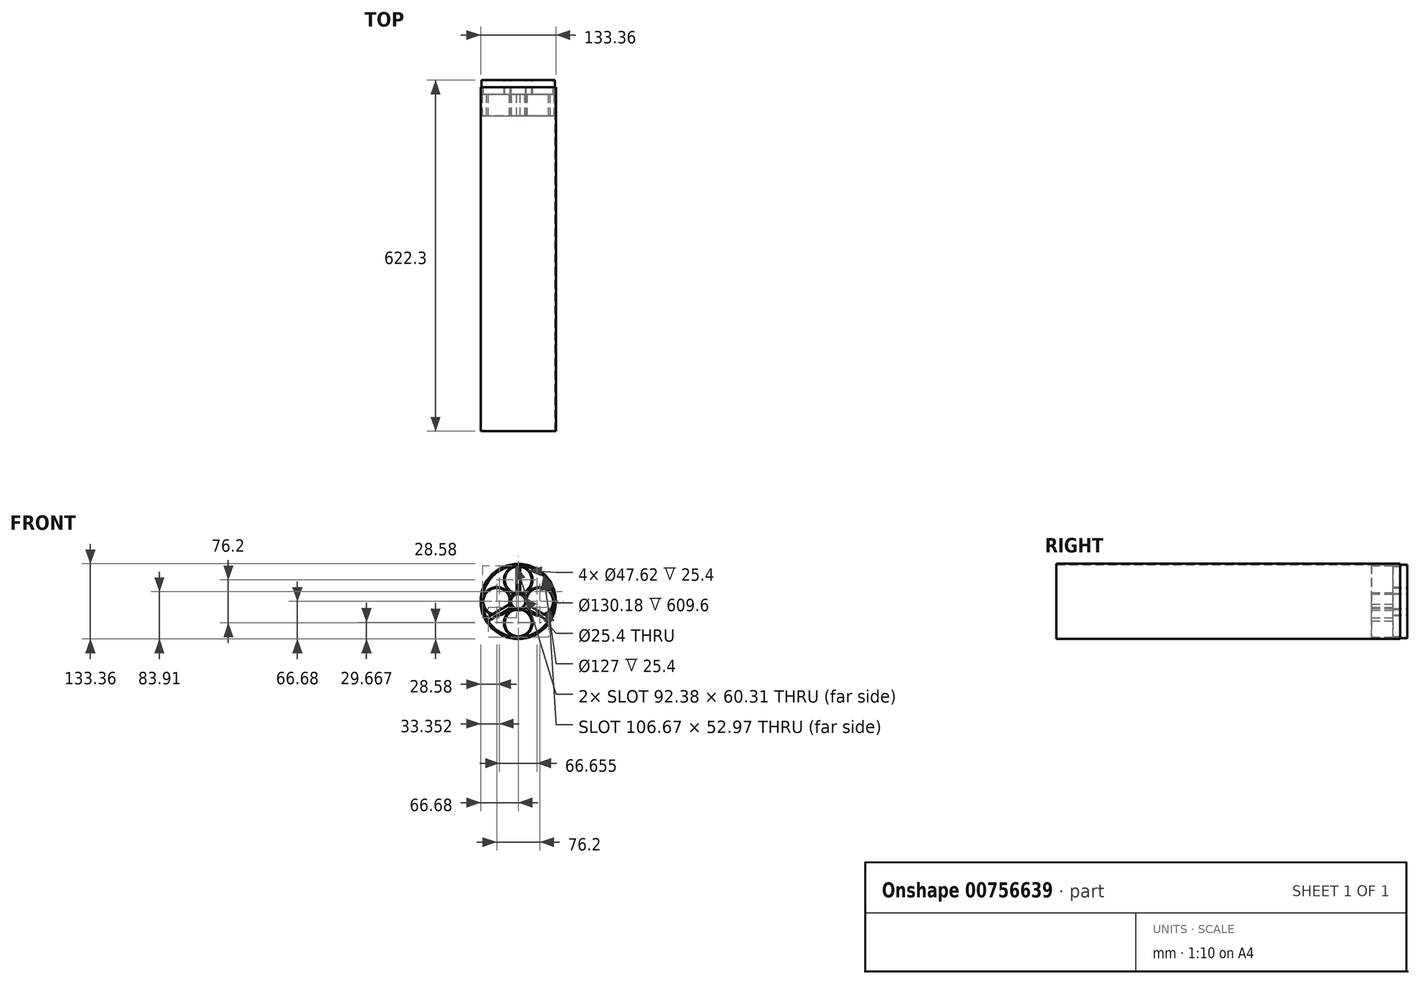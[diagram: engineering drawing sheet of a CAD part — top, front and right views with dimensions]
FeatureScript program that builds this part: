
annotation { "Feature Type Name" : "Feature", "Feature Type Description" : "" }
export const myFeature = defineFeature(function(context is Context, id is Id, definition is map)
    precondition{}
    {
        {
            var Q0;
            Q0=qCreatedBy(makeId("Front.planeOp"),FACE);
            var sketch = newSketch(context, id + "F0", { "sketchPlane" : qUnion([Q0])});
            skCircle(sketch, "E0", {"center": v(0, 0) * mm, "radius": 63.5 * mm});
            skCircle(sketch, "E1", {"center": v(0, 0) * mm, "radius": 12.7 * mm});
            skLineSegment(sketch, "E2", {"start": v(0, 63.5) * mm, "end": v(0, 12.7) * mm});
            skCircle(sketch, "E3", {"center": v(0, 38.1) * mm, "radius": 25.4 * mm});
            skCircle(sketch, "E4.1.0", {"center": v(-38.1, 0) * mm, "radius": 25.4 * mm});
            skCircle(sketch, "E4.2.0", {"center": v(0, -38.1) * mm, "radius": 25.4 * mm});
            skCircle(sketch, "E4.3.0", {"center": v(38.1, 0) * mm, "radius": 25.4 * mm});
            skCircle(sketch, "E5.0", {"center": v(0, 0) * mm, "radius": 65.09 * mm});
            skCircle(sketch, "E6.0", {"center": v(-38.1, 0) * mm, "radius": 23.81 * mm});
            skCircle(sketch, "E7.0", {"center": v(0, 38.1) * mm, "radius": 23.81 * mm});
            skCircle(sketch, "E8.0", {"center": v(38.1, 0) * mm, "radius": 23.81 * mm});
            skCircle(sketch, "E9.0", {"center": v(0, -38.1) * mm, "radius": 23.81 * mm});
            skCircle(sketch, "E10.0", {"center": v(0, 0) * mm, "radius": 66.68 * mm});
            skSolve(sketch);
        }
        {
            var Q0;
            {var subQ1=sQuery(id+"F0.wireOp",EDGE,"E2");var subQ3=sQuery(id+"F0.wireOp",EDGE,"E7.0");var subQ4=makeQuery(id+"F0.imprint","INTERSECT",VERTEX,{"disambiguationData":[OD(0.0)],"derivedFrom":[subQ1,subQ3]});Q0=makeQuery(id+"F0.imprint","IMPRINT",FACE,{"disambiguationData":[TD([[makeQuery(id+"F0.imprint","IMPRINT",EDGE,{"disambiguationData":[TD([[subQ4,1.0]])],"derivedFrom":subQ3}),-1.0]])]});}
            var Q1;
            Q1=makeQuery(id+"F0.imprint","IMPRINT",FACE,{"disambiguationData":[TD([[makeQuery(id+"F0.imprint","IMPRINT",EDGE,{"derivedFrom":sQuery(id+"F0.wireOp",EDGE,"E8.0")}),-1.0]])]});
            var Q2;
            Q2=makeQuery(id+"F0.imprint","IMPRINT",FACE,{"disambiguationData":[TD([[makeQuery(id+"F0.imprint","IMPRINT",EDGE,{"derivedFrom":sQuery(id+"F0.wireOp",EDGE,"E9.0")}),-1.0]])]});
            var Q3;
            {var subQ1=sQuery(id+"F0.wireOp",EDGE,"E2");var subQ3=sQuery(id+"F0.wireOp",EDGE,"E7.0");var subQ4=makeQuery(id+"F0.imprint","INTERSECT",VERTEX,{"disambiguationData":[OD(0.0)],"derivedFrom":[subQ1,subQ3]});Q3=makeQuery(id+"F0.imprint","IMPRINT",FACE,{"disambiguationData":[TD([[makeQuery(id+"F0.imprint","IMPRINT",EDGE,{"disambiguationData":[TD([[subQ4,-1.0]])],"derivedFrom":subQ3}),-1.0]])]});}
            var Q4;
            Q4=makeQuery(id+"F0.imprint","IMPRINT",FACE,{"disambiguationData":[TD([[makeQuery(id+"F0.imprint","IMPRINT",EDGE,{"derivedFrom":sQuery(id+"F0.wireOp",EDGE,"E6.0")}),-1.0]])]});
            var Q5;
            Q5=makeQuery(id+"F0.imprint","IMPRINT",FACE,{"disambiguationData":[TD([[makeQuery(id+"F0.imprint","IMPRINT",EDGE,{"derivedFrom":sQuery(id+"F0.wireOp",EDGE,"E5.0")}),1.0]])]});
            extrude(context, id + "F1", {"entities" : qUnion([Q0, Q1, Q2, Q3, Q4, Q5]), "endBound" : BoundingType.SYMMETRIC, "depth" : 25.4 * mm, "offsetDistance" : 25.4 * mm});
        }
        {
            var Q0;
            Q0=qCreatedBy(makeId("Front.planeOp"),FACE);
            var sketch = newSketch(context, id + "F2", { "sketchPlane" : qUnion([Q0])});
            skArc(sketch, "E11", {"start": v(-53.34, -34.46) * mm, "mid": v(0, -63.5) * mm, "end": v(53.34, -34.46) * mm});
            skCircle(sketch, "E12", {"center": v(0, 0) * mm, "radius": 12.7 * mm});
            skCircle(sketch, "E13.0", {"center": v(0, 0) * mm, "radius": 65.09 * mm});
            skLineSegment(sketch, "E14.0", {"start": v(-53.4, -34.5) * mm, "end": v(-11.88, -10.53) * mm});
            skLineSegment(sketch, "E15.0", {"start": v(-56.58, -29) * mm, "end": v(-15.06, -5.03) * mm});
            skLineSegment(sketch, "E16.0", {"start": v(56.58, -29) * mm, "end": v(15.06, -5.03) * mm});
            skLineSegment(sketch, "E17.0", {"start": v(53.4, -34.5) * mm, "end": v(11.88, -10.53) * mm});
            skLineSegment(sketch, "E18.0", {"start": v(-3.17, 63.5) * mm, "end": v(-3.17, 15.55) * mm});
            skLineSegment(sketch, "E19.0", {"start": v(3.18, 63.5) * mm, "end": v(3.18, 15.55) * mm});
            skArc(sketch, "E20.0", {"start": v(-11.88, -10.53) * mm, "mid": v(0, -15.88) * mm, "end": v(11.88, -10.53) * mm});
            skPoint(sketch, "E21.orphan", {"position": v(-55, -31.75) * mm});
            skPoint(sketch, "E22.orphan", {"position": v(55, -31.75) * mm});
            skPoint(sketch, "E23.orphan", {"position": v(0, 63.5) * mm});
            skArc(sketch, "E24.trimOffspring", {"start": v(-3.17, 15.55) * mm, "mid": v(-13.75, 7.94) * mm, "end": v(-15.06, -5.03) * mm});
            skArc(sketch, "E25.trimOffspring", {"start": v(-3.17, 63.42) * mm, "mid": v(-55, 31.75) * mm, "end": v(-56.51, -28.96) * mm});
            skArc(sketch, "E26.trimOffspring", {"start": v(15.06, -5.03) * mm, "mid": v(13.75, 7.94) * mm, "end": v(3.18, 15.55) * mm});
            skArc(sketch, "E27.trimOffspring", {"start": v(56.51, -28.96) * mm, "mid": v(55, 31.75) * mm, "end": v(3.18, 63.42) * mm});
            skSolve(sketch);
        }
        {
            var Q0;
            Q0=makeQuery(id+"F2.imprint","IMPRINT",FACE,{"disambiguationData":[TD([[makeQuery(id+"F2.imprint","IMPRINT",EDGE,{"derivedFrom":sQuery(id+"F2.wireOp",EDGE,"E12")}),1.0]])]});
            extrude(context, id + "F3", {"entities" : qUnion([Q0]), "depth" : 50.8 * mm, "offsetDistance" : 25.4 * mm});
        }
        {
            var Q0;
            {var subQ8=sQuery(id+"F2.wireOp",EDGE,"E11");Q0=makeQuery(id+"F2.imprint","IMPRINT",FACE,{"disambiguationData":[TD([[makeQuery(id+"F2.imprint","IMPRINT",EDGE,{"derivedFrom":subQ8}),-1.0]])]});}
            extrude(context, id + "F4", {"entities" : qUnion([Q0]), "depth" : 50.8 * mm, "offsetDistance" : 25.4 * mm, "hasSecondDirection" : true, "secondDirectionOppositeDirection" : false, "secondDirectionDepth" : 12.7 * mm});
        }
        {
            var Q0;
            Q0=makeQuery(id+"F0.imprint","IMPRINT",FACE,{"disambiguationData":[TD([[makeQuery(id+"F0.imprint","IMPRINT",EDGE,{"derivedFrom":sQuery(id+"F0.wireOp",EDGE,"E5.0")}),-1.0]])]});
            extrude(context, id + "F5", {"entities" : qUnion([Q0]), "depth" : 609.6 * mm, "offsetDistance" : 25.4 * mm});
        }
    });
